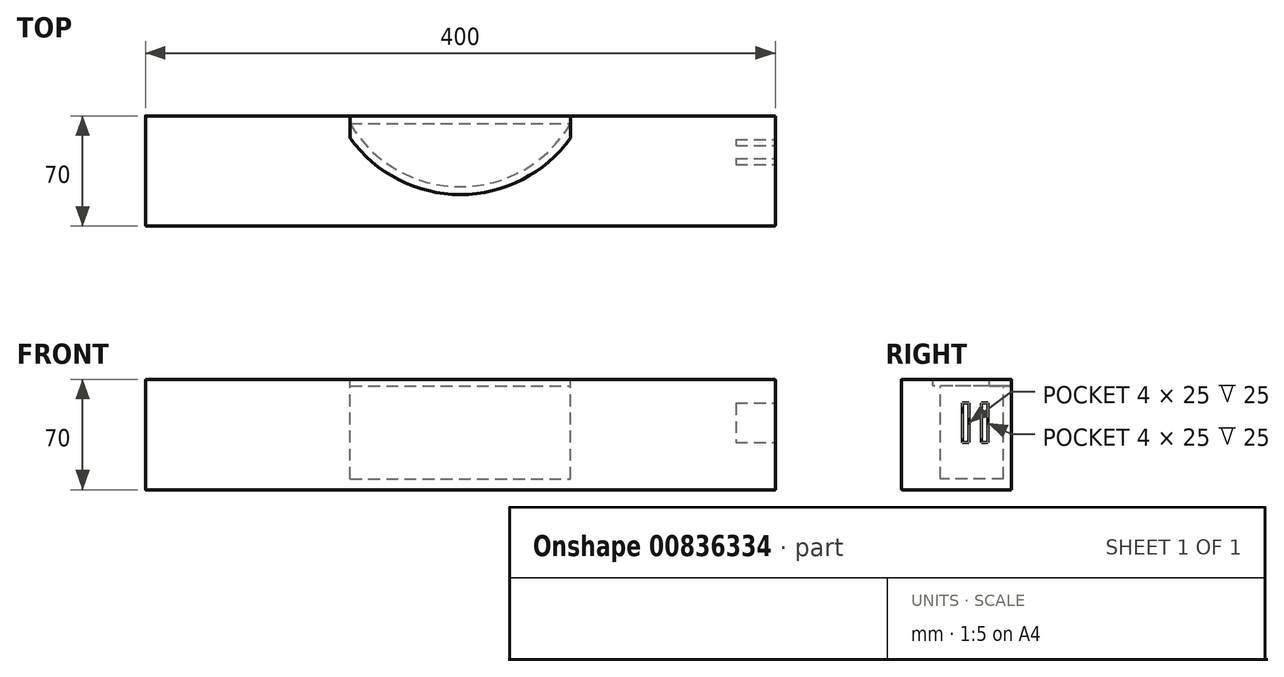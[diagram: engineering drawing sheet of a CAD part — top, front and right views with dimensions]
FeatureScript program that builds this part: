
annotation { "Feature Type Name" : "Feature", "Feature Type Description" : "" }
export const myFeature = defineFeature(function(context is Context, id is Id, definition is map)
    precondition{}
    {
        {
            var Q0;
            Q0=qCreatedBy(makeId("Top.planeOp"),FACE);
            var sketch = newSketch(context, id + "F0", { "sketchPlane" : qUnion([Q0])});
            skLineSegment(sketch, "E0.bottom", {"start": v(0, 0) * mm, "end": v(400, 0) * mm});
            skLineSegment(sketch, "E0.top", {"start": v(0, -70) * mm, "end": v(400, -70) * mm});
            skLineSegment(sketch, "E0.left", {"start": v(0, 0) * mm, "end": v(0, -70) * mm});
            skLineSegment(sketch, "E0.right", {"start": v(400, 0) * mm, "end": v(400, -70) * mm});
            skSolve(sketch);
        }
        {
            var Q0;
            Q0 = qSketchRegion(id + "F0", true);
            extrude(context, id + "F1", {"entities" : qUnion([Q0]), "depth" : 70 * mm, "offsetDistance" : 25 * mm});
        }
        {
            var Q0;
            Q0=makeQuery(id+"F1.opExtrude","CAP_FACE",FACE,{"disambiguationData":[OSD([sQuery(id+"F0.wireOp",EDGE,"E0.bottom"),sQuery(id+"F0.wireOp",EDGE,"E0.top"),sQuery(id+"F0.wireOp",EDGE,"E0.left"),sQuery(id+"F0.wireOp",EDGE,"E0.right")])],"isStart":false});
            var sketch = newSketch(context, id + "F2", { "sketchPlane" : qUnion([Q0])});
            skPoint(sketch, "E1", {"position": v(200, 0) * mm});
            skArc(sketch, "E2", {"start": v(130, -5) * mm, "mid": v(200, -45) * mm, "end": v(270, -5) * mm});
            skLineSegment(sketch, "E3", {"start": v(270, -5) * mm, "end": v(270, 0) * mm, "construction": true});
            skLineSegment(sketch, "E4", {"start": v(270, 0) * mm, "end": v(130, 0) * mm, "construction": true});
            skLineSegment(sketch, "E5", {"start": v(130, 0) * mm, "end": v(130, -5) * mm, "construction": true});
            skLineSegment(sketch, "E6", {"start": v(270, -5) * mm, "end": v(130, -5) * mm});
            skPoint(sketch, "E7", {"position": v(200, -45) * mm});
            skSolve(sketch);
        }
        {
            var Q0;
            Q0 = qSketchRegion(id + "F2", true);
            extrude(context, id + "F3", {"entities" : qUnion([Q0]), "operationType" : NewBodyOperationType.REMOVE, "endBound" : BoundingType.UP_TO_NEXT, "oppositeDirection" : true, "depth" : 25 * mm, "hasOffset" : true, "offsetDistance" : 7 * mm});
        }
        {
            var Q0;
            Q0=makeQuery(id+"F1.opExtrude","CAP_FACE",FACE,{"disambiguationData":[OSD([sQuery(id+"F0.wireOp",EDGE,"E0.bottom"),sQuery(id+"F0.wireOp",EDGE,"E0.top"),sQuery(id+"F0.wireOp",EDGE,"E0.left"),sQuery(id+"F0.wireOp",EDGE,"E0.right")])],"isStart":false});
            var sketch = newSketch(context, id + "F4", { "sketchPlane" : qUnion([Q0])});
            skArc(sketch, "E8.0", {"start": v(130, -14.14) * mm, "mid": v(200, -50) * mm, "end": v(270, -14.14) * mm});
            skLineSegment(sketch, "E9", {"start": v(270, -14.14) * mm, "end": v(270, 0) * mm});
            skLineSegment(sketch, "E10", {"start": v(270, 0) * mm, "end": v(130, 0) * mm});
            skLineSegment(sketch, "E11", {"start": v(130, 0) * mm, "end": v(130, -14.14) * mm});
            skSolve(sketch);
        }
        {
            var Q0;
            Q0 = qSketchRegion(id + "F4", true);
            extrude(context, id + "F5", {"entities" : qUnion([Q0]), "operationType" : NewBodyOperationType.REMOVE, "oppositeDirection" : true, "depth" : 4 * mm, "offsetDistance" : 25 * mm});
        }
        {
            var Q0;
            Q0=makeQuery(id+"F1.opExtrude","SWEPT_FACE",FACE,{"disambiguationData":[OSD([sQuery(id+"F0.wireOp",EDGE,"E0.right")])]});
            var sketch = newSketch(context, id + "F6", { "sketchPlane" : qUnion([Q0])});
            skLineSegment(sketch, "E12.bottom", {"start": v(-15, 55) * mm, "end": v(-19, 55) * mm});
            skLineSegment(sketch, "E12.top", {"start": v(-15, 30) * mm, "end": v(-19, 30) * mm});
            skLineSegment(sketch, "E12.left", {"start": v(-15, 55) * mm, "end": v(-15, 30) * mm});
            skLineSegment(sketch, "E12.right", {"start": v(-19, 55) * mm, "end": v(-19, 30) * mm});
            skLineSegment(sketch, "E13.bottom", {"start": v(-27, 55) * mm, "end": v(-31, 55) * mm});
            skLineSegment(sketch, "E13.top", {"start": v(-27, 30) * mm, "end": v(-31, 30) * mm});
            skLineSegment(sketch, "E13.left", {"start": v(-27, 55) * mm, "end": v(-27, 30) * mm});
            skLineSegment(sketch, "E13.right", {"start": v(-31, 55) * mm, "end": v(-31, 30) * mm});
            skSolve(sketch);
        }
        {
            var Q0;
            Q0 = qSketchRegion(id + "F6", true);
            extrude(context, id + "F7", {"entities" : qUnion([Q0]), "operationType" : NewBodyOperationType.REMOVE, "oppositeDirection" : true, "depth" : 25 * mm, "offsetDistance" : 25 * mm});
        }
        {
            var Q0;
            Q0=makeQuery(id+"F1.opExtrude","CAP_FACE",FACE,{"disambiguationData":[OSD([sQuery(id+"F0.wireOp",EDGE,"E0.bottom"),sQuery(id+"F0.wireOp",EDGE,"E0.top"),sQuery(id+"F0.wireOp",EDGE,"E0.left"),sQuery(id+"F0.wireOp",EDGE,"E0.right")])],"isStart":false});
            var sketch = newSketch(context, id + "F8", { "sketchPlane" : qUnion([Q0])});
            skArc(sketch, "E14", {"start": v(130, -14.14) * mm, "mid": v(200, -50) * mm, "end": v(270, -14.14) * mm});
            skLineSegment(sketch, "E15", {"start": v(130, -14.14) * mm, "end": v(130, 0) * mm});
            skLineSegment(sketch, "E16", {"start": v(130, 0) * mm, "end": v(270, 0) * mm});
            skLineSegment(sketch, "E17", {"start": v(270, 0) * mm, "end": v(270, -14.14) * mm});
            skSolve(sketch);
        }
        {
            var Q0;
            Q0 = qSketchRegion(id + "F8", true);
            extrude(context, id + "F9", {"entities" : qUnion([Q0]), "oppositeDirection" : true, "depth" : 4 * mm, "offsetDistance" : 25 * mm});
        }
        {
            var Q0;
            Q0=makeQuery(id+"F1.opExtrude","CAP_EDGE",EDGE,{"disambiguationData":[OSD([sQuery(id+"F0.wireOp",EDGE,"E0.left")])],"isStart":false});
            var Q1;
            Q1=makeQuery(id+"F1.opExtrude","CAP_EDGE",EDGE,{"disambiguationData":[OSD([sQuery(id+"F0.wireOp",EDGE,"E0.top")])],"isStart":false});
            var Q2;
            Q2=makeQuery(id+"F1.opExtrude","CAP_EDGE",EDGE,{"disambiguationData":[OSD([sQuery(id+"F0.wireOp",EDGE,"E0.right")])],"isStart":false});
            var Q3;
            Q3=makeQuery(id+"F1.opExtrude","SWEPT_FACE",FACE,{"disambiguationData":[OSD([sQuery(id+"F0.wireOp",EDGE,"E0.top")])]});
            fillet(context, id + "F10", {"entities" : qUnion([Q0, Q1, Q2, Q3]), "radius" : 0.5 * mm, "tangentPropagation" : true, "allowEdgeOverflow" : false});
        }
    });
